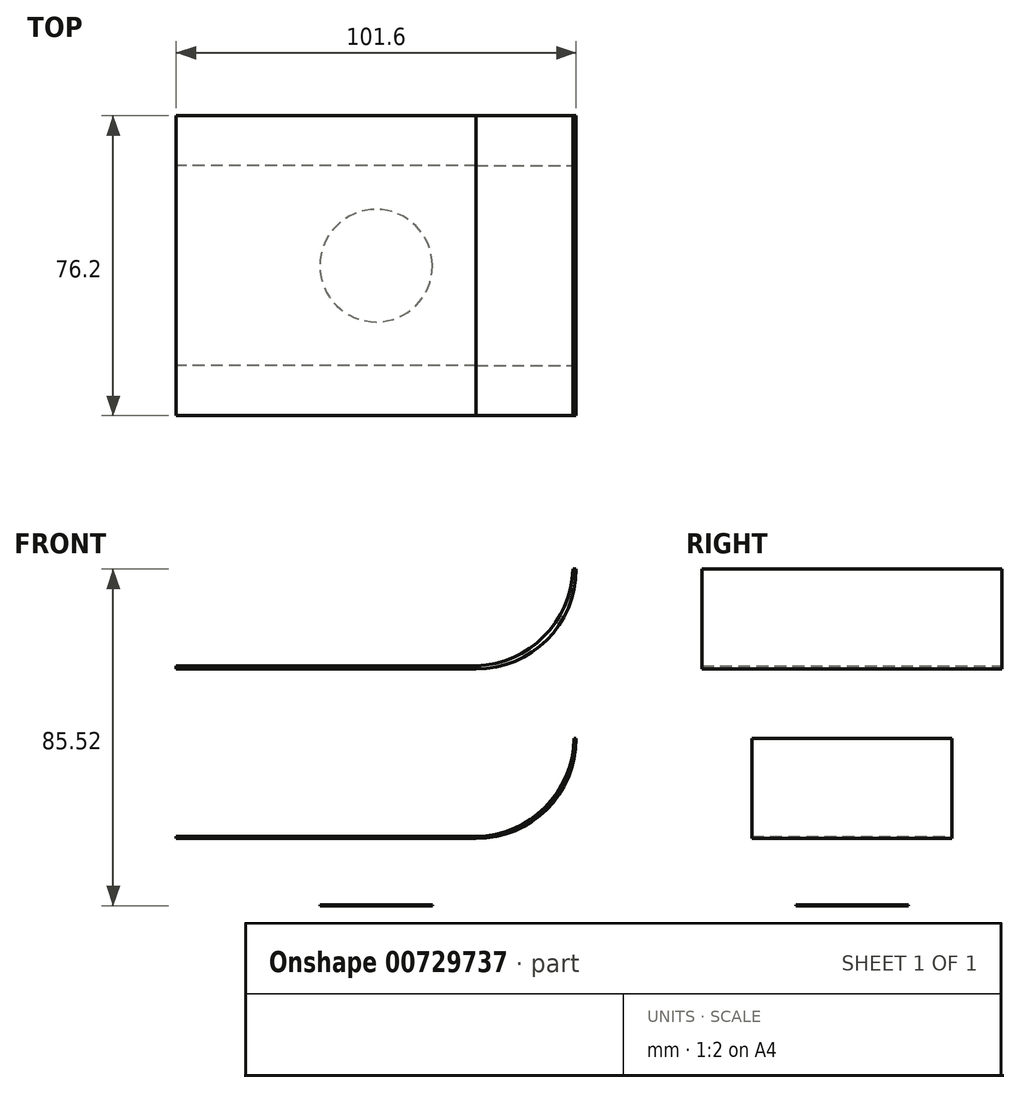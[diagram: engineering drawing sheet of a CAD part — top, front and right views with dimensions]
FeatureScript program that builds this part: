
annotation { "Feature Type Name" : "Feature", "Feature Type Description" : "" }
export const myFeature = defineFeature(function(context is Context, id is Id, definition is map)
    precondition{}
    {
        {
            var Q0;
            Q0=qCreatedBy(makeId("Top.planeOp"),FACE);
            var sketch = newSketch(context, id + "F0", { "sketchPlane" : qUnion([Q0])});
            skCircle(sketch, "E0", {"center": v(0, 0) * mm, "radius": 14.29 * mm});
            skSolve(sketch);
        }
        {
            var Q0;
            Q0=qSketchRegion(id+"F0",true);
            extrude(context, id + "F1", {"entities" : qUnion([Q0]), "depth" : 0.25 * mm});
        }
        {
            var Q0;
            Q0=qCreatedBy(makeId("Front.planeOp"),FACE);
            var sketch = newSketch(context, id + "F2", { "sketchPlane" : qUnion([Q0])});
            skLineSegment(sketch, "E1.bottom", {"start": v(50.8, 42.47) * mm, "end": v(50.3, 42.47) * mm});
            skLineSegment(sketch, "E1.top", {"start": v(25.4, 17.07) * mm, "end": v(-50.8, 17.07) * mm});
            skLineSegment(sketch, "E1.left", {"start": v(50.8, 42.47) * mm, "end": v(50.8, 42.47) * mm});
            skLineSegment(sketch, "E1.right", {"start": v(-50.8, 17.57) * mm, "end": v(-50.8, 17.07) * mm});
            skPoint(sketch, "E1.middle", {"position": v(0, 29.77) * mm});
            skPoint(sketch, "E2", {"position": v(28.14, 29.77) * mm});
            skPoint(sketch, "E3", {"position": v(28.14, 17.07) * mm});
            skPoint(sketch, "E4", {"position": v(28.14, 42.47) * mm});
            skPoint(sketch, "E5.visualSharp", {"position": v(50.8, 17.07) * mm});
            skArc(sketch, "E5.filletArc", {"start": v(25.4, 17.07) * mm, "mid": v(43.36, 24.5) * mm, "end": v(50.8, 42.47) * mm});
            skArc(sketch, "E6", {"start": v(25.4, 17.57) * mm, "mid": v(42.86, 25) * mm, "end": v(50.3, 42.47) * mm});
            skLineSegment(sketch, "E7", {"start": v(25.4, 17.57) * mm, "end": v(-50.8, 17.57) * mm});
            skPoint(sketch, "E8.orphan", {"position": v(-50.8, 42.47) * mm});
            skSolve(sketch);
        }
        {
            var Q0;
            Q0=qSketchRegion(id+"F2",true);
            extrude(context, id + "F3", {"entities" : qUnion([Q0]), "depth" : 50.8 * mm, "symmetric" : true});
        }
        {
            var Q0;
            Q0=qCreatedBy(makeId("Front.planeOp"),FACE);
            var sketch = newSketch(context, id + "F4", { "sketchPlane" : qUnion([Q0])});
            skLineSegment(sketch, "E9.bottom", {"start": v(25.4, 60.12) * mm, "end": v(-50.8, 60.12) * mm});
            skLineSegment(sketch, "E9.top", {"start": v(50.8, 85.52) * mm, "end": v(49.99, 85.52) * mm});
            skLineSegment(sketch, "E9.left", {"start": v(50.8, 85.52) * mm, "end": v(50.8, 85.52) * mm});
            skLineSegment(sketch, "E9.right", {"start": v(-50.8, 60.12) * mm, "end": v(-50.8, 60.93) * mm});
            skPoint(sketch, "E9.middle", {"position": v(0, 72.82) * mm});
            skPoint(sketch, "E10.visualSharp", {"position": v(50.8, 60.12) * mm});
            skArc(sketch, "E10.filletArc", {"start": v(25.4, 60.12) * mm, "mid": v(43.36, 67.56) * mm, "end": v(50.8, 85.52) * mm});
            skArc(sketch, "E11", {"start": v(25.4, 60.93) * mm, "mid": v(42.56, 68.36) * mm, "end": v(49.99, 85.52) * mm});
            skLineSegment(sketch, "E12", {"start": v(25.4, 60.93) * mm, "end": v(-50.8, 60.93) * mm});
            skPoint(sketch, "E13.trimOffspring.end.orphan", {"position": v(-50.8, 85.52) * mm});
            skSolve(sketch);
        }
        {
            var Q0;
            Q0=qSketchRegion(id+"F4",true);
            extrude(context, id + "F5", {"entities" : qUnion([Q0]), "depth" : 76.2 * mm, "symmetric" : true});
        }
    });
